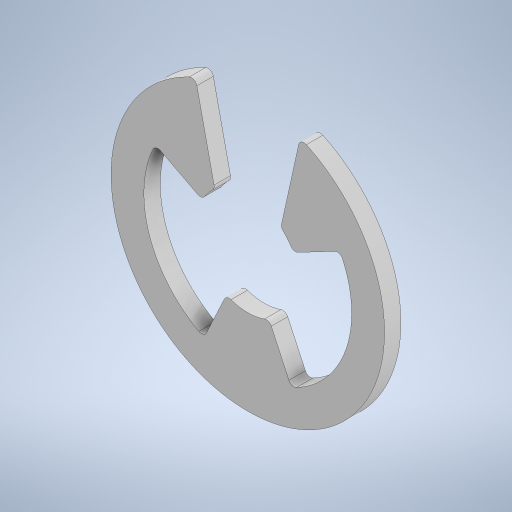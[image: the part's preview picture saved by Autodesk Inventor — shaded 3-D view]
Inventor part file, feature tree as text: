
AUTODESK INVENTOR PART (.ipt)
format: ipt  version: 2024 (Build 280153000, 153)  size: 299,520 bytes
history: native  units: in
note: dims shown in document units (in); Inventor stores cm internally (conversion verified against a paired STEP export)
features: extrude x3, sketch x3, projected_geometry x2, fillet x1, direct_edit x1, other x1
ambient origin geometry x8: Origin, YZ Plane, XZ Plane, XY Plane, X Axis, Y Axis, Z Axis, Center Point
bodies: Solid1 (feature_tree)
feature tree (11):
  extrude  "Extrusion1"  Depth=0.25in
  extrude  "Extrusion2"  Depth=0.05in
  extrude  "Extrusion3"  Depth=0.3937in
  fillet  "Fillet1"  Radius=0.015in
  direct_edit  "Direct Edit1"
  sketch  "Sketch1"  dims[d0=0.0938in d1=0.25in]
  sketch  "Sketch2"  dims[d2=0.015in d3=0.0in d4=0.05in]
  sketch  "Sketch3"  dims[d5=0.1in d6=0.1718in d7=0.015in d8=0.0in d9=0.03in d10=0.3436in d11=0.3436in d12=0.0832in d13=0.039in d14=0.015in d15=0.0in d16=0.005in d17=3.937in d18=0.3937in d19=0.3937in]
  projected_geometry  "Project Cut Edges1"
  projected_geometry  "Project Cut Edges2"
  other  "Scale1"
